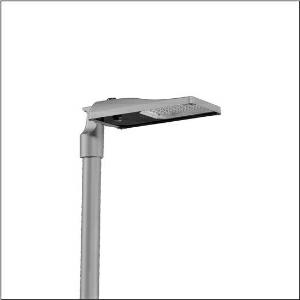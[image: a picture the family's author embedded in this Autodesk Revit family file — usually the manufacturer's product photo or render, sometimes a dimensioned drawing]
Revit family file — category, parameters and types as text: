
# Revit family: streetlight_sl_31_mini___stw1_0a_5xh6e31t08ha_3957
name_source: partatom
category: Lighting Fixtures
units: mm (PartAtom-declared; Revit-internal decimal feet)

## family parameters
Cut with Voids When Loaded = No
Host = Face
Light Source = No
Part Type = Normal
Room Calculation Point = No
Round Connector Dimension = Use Diameter
Shared = No

## types (1)
- --- (1 x LED, 9230 lm, 68.3 W, 3000K)
    Apparent Load = 68 VA
    CIE Flux Codes = 38 75 98 100 100
    Color Rendering = 70
    Color Temperature = 3000K
    Default Elevation = 1800 mm
    Description = Streetlight SL 31 mini D4i, Desk-Remote mast luminaire for post-top, side-entry; light control with lens of PMMA; light distribution: STW1.0a, direct asymmetric distribution, for standard-compliant lighting for roads and squares; LED: luminous flux: 9.230lm, light colour: 730, colour temperature: 3000K; luminous efficacy: 135,1lm/W; control: pre-setting: logarithmic dimming characteristic, flexible luminous flux parameterisation, time-dependent luminous flux control, constant luminous flux control, power reduction, intelligent temperature release in ECG and LED module, overheat protection; luminaire housing, of diecast aluminium, Siteco® metallic grey (DB 702S), corrosivity category C5 high according to DIN EN ISO 12944; cover of toughened safety glass, transparent, opened without tools; mast flange of diecast aluminium, Siteco® metallic grey (DB 702S), spigot size: 76/60mm, mast flange included unmounted; with cable H07RN-F 2x 1.5mm², cable length: 8,5m, connection cable pre-assembled; mains connection: 220..240V, AC, 50/60Hz; power consumption (at start of service life): 68,3W / (at end of service life): 74,5W / (with reduced operation 50%): 29,5W; protection rating (complete): IP66; insulation class (complete): insulation class II (safety insulation); impact resistance: IK09; certification: CE, ENEC, ENEC+, VDE, UKCA, ZD4i; permissible operating ambient temperature for outdoor applications: -40..+50°C; packaging unit: 1 piece

Light Distribution: STW1.0a
    Height = 76 mm
    Lamp = 1 x LED
    Lamp Light Flux = 9230 lm
    Lamp Power = 68.3 W
    Lamp count = 1
    Length = 547 mm
    Luminous efficacy = 135 lm/W
    Manufacturer = Siteco
    ModVariant = No
    Model = 5XH6E31T08HA
    Number of Poles = 1
    OnlyDefault = Yes
    Power Factor = 1
    Product Name = Streetlight SL 31 mini | STW1.0a
    Product group = mast luminaire | pylon top
    ProductGroupID = 6100
    Protection Class = Protection class II
    Protection Degree = IP 66
    RLX_Detail_Level = 1
    RLX_Emergency_Light_Flux = 0 lm
    RLX_Emergency_Type = 0
    RLX_Emergency_Type_DB = No
    RlxData = <blob elided: 24385 chars, md5=e090de18>
    Socket = socket
    Standby Power = 0 W
    System Light Flux = 9230 lm
    System Power = 68 W
    Type Comments = factory setting: luminous flux: 100 % | dim-lin: 254 | 692 mA
    Type Image = l_1300332.jpg
    URL = http://relux.com
    VarID = @adj_019037
    Voltage = 0 V
    Weight = 0.00 kg
    Width = 265 mm

## geometry (parser evidence)
native form markers: Blend x4, Sweep x9
no freeform markers — native parametric forms only
